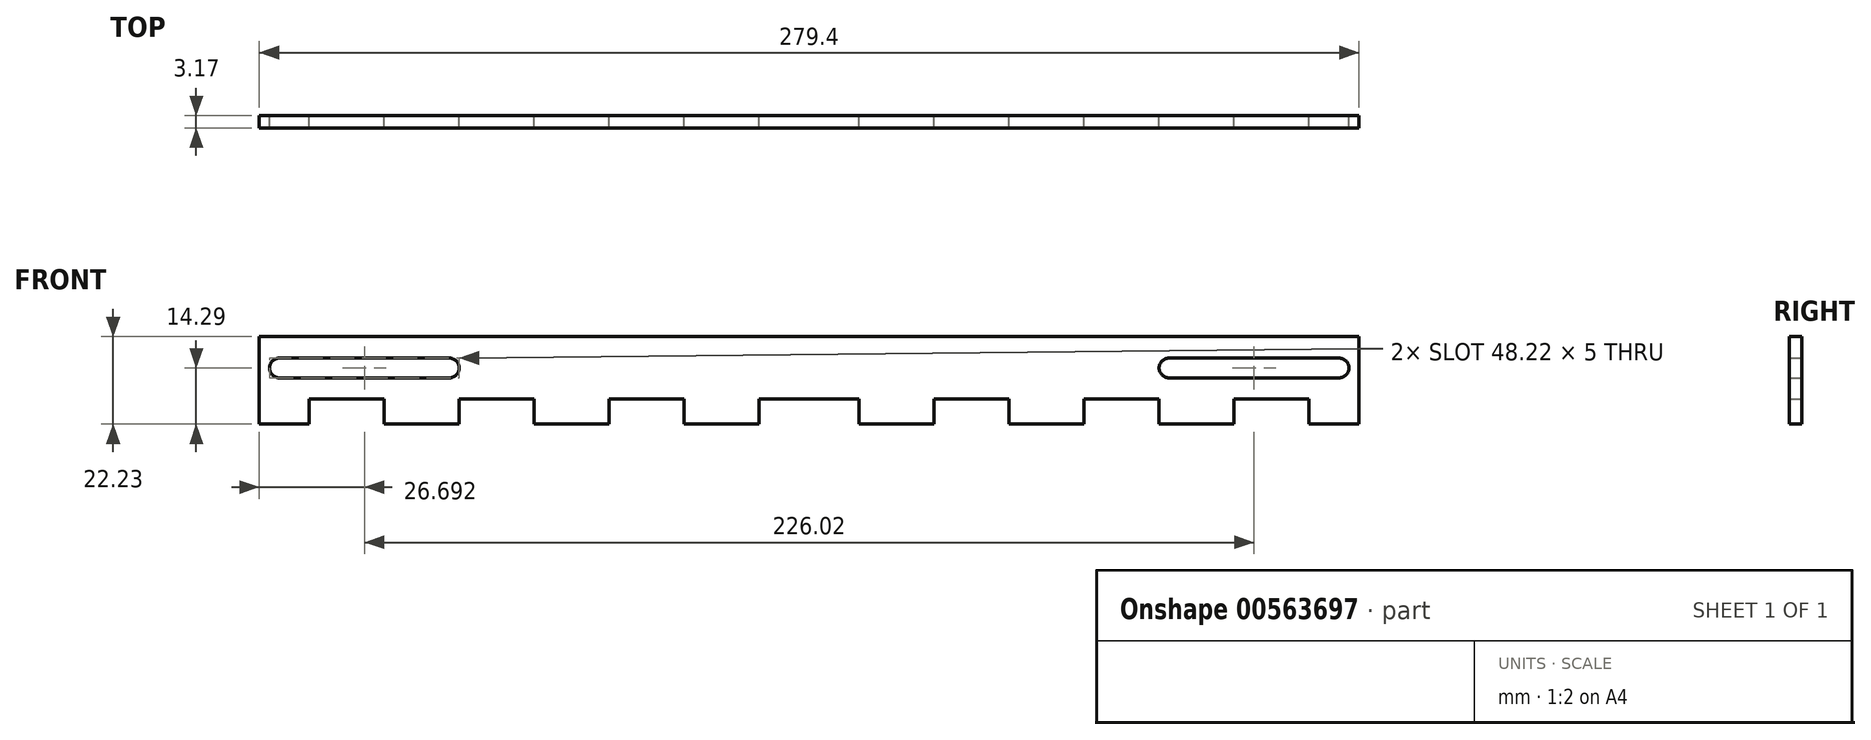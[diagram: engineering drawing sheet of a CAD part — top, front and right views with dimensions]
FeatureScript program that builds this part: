
annotation { "Feature Type Name" : "Feature", "Feature Type Description" : "" }
export const myFeature = defineFeature(function(context is Context, id is Id, definition is map)
    precondition{}
    {
        {
            var Q0;
            Q0=qCreatedBy(makeId("Front.planeOp"),FACE);
            var sketch = newSketch(context, id + "F0", { "sketchPlane" : qUnion([Q0])});
            skLineSegment(sketch, "E0", {"start": v(-38.69, 19.05) * mm, "end": v(-38.69, -20.37) * mm, "construction": true});
            skLineSegment(sketch, "E1", {"start": v(-165.69, -7.94) * mm, "end": v(-165.69, -1.59) * mm});
            skLineSegment(sketch, "E2", {"start": v(-165.69, -1.59) * mm, "end": v(-146.64, -1.59) * mm});
            skLineSegment(sketch, "E3.1.0.0", {"start": v(-146.64, -1.59) * mm, "end": v(-146.64, -7.94) * mm});
            skLineSegment(sketch, "E3.1.0.1", {"start": v(-146.64, -7.94) * mm, "end": v(-127.59, -7.94) * mm});
            skLineSegment(sketch, "E3.1.0.2", {"start": v(-127.59, -7.94) * mm, "end": v(-127.59, -1.59) * mm});
            skLineSegment(sketch, "E3.1.0.3", {"start": v(-127.59, -1.59) * mm, "end": v(-108.54, -1.59) * mm});
            skLineSegment(sketch, "E3.2.0.0", {"start": v(-108.54, -1.59) * mm, "end": v(-108.54, -7.94) * mm});
            skLineSegment(sketch, "E3.2.0.1", {"start": v(-108.54, -7.94) * mm, "end": v(-89.49, -7.94) * mm});
            skLineSegment(sketch, "E3.2.0.2", {"start": v(-89.49, -7.94) * mm, "end": v(-89.49, -1.59) * mm});
            skLineSegment(sketch, "E3.2.0.3", {"start": v(-89.49, -1.59) * mm, "end": v(-70.44, -1.59) * mm});
            skLineSegment(sketch, "E3.3.0.0", {"start": v(-70.44, -1.59) * mm, "end": v(-70.44, -7.94) * mm});
            skLineSegment(sketch, "E3.3.0.1", {"start": v(-70.44, -7.94) * mm, "end": v(-51.39, -7.94) * mm});
            skLineSegment(sketch, "E3.3.0.2", {"start": v(-51.39, -7.94) * mm, "end": v(-51.39, -1.59) * mm});
            skLineSegment(sketch, "E4.MirrorCS", {"start": v(12.11, -7.94) * mm, "end": v(12.11, -1.59) * mm});
            skLineSegment(sketch, "E5.MirrorCS", {"start": v(-6.94, -1.59) * mm, "end": v(-6.94, -7.94) * mm});
            skLineSegment(sketch, "E6.MirrorCS", {"start": v(69.26, -1.59) * mm, "end": v(69.26, -7.94) * mm});
            skLineSegment(sketch, "E7.MirrorCS", {"start": v(50.21, -7.94) * mm, "end": v(50.21, -1.59) * mm});
            skLineSegment(sketch, "E8.MirrorCS", {"start": v(31.16, -1.59) * mm, "end": v(31.16, -7.94) * mm});
            skLineSegment(sketch, "E9.MirrorCS", {"start": v(88.31, -7.94) * mm, "end": v(88.31, -1.59) * mm});
            skLineSegment(sketch, "E10.MirrorCS", {"start": v(-25.99, -7.94) * mm, "end": v(-25.99, -1.59) * mm});
            skLineSegment(sketch, "E11.MirrorCS", {"start": v(-6.94, -7.94) * mm, "end": v(-25.99, -7.94) * mm});
            skLineSegment(sketch, "E12.MirrorCS", {"start": v(88.31, -1.59) * mm, "end": v(69.26, -1.59) * mm});
            skLineSegment(sketch, "E13.MirrorCS", {"start": v(12.11, -1.59) * mm, "end": v(-6.94, -1.59) * mm});
            skLineSegment(sketch, "E14.MirrorCS", {"start": v(50.21, -1.59) * mm, "end": v(31.16, -1.59) * mm});
            skLineSegment(sketch, "E15.MirrorCS", {"start": v(31.16, -7.94) * mm, "end": v(12.11, -7.94) * mm});
            skLineSegment(sketch, "E16.MirrorCS", {"start": v(69.26, -7.94) * mm, "end": v(50.21, -7.94) * mm});
            skLineSegment(sketch, "E17", {"start": v(-51.39, -1.59) * mm, "end": v(-25.99, -1.59) * mm});
            skLineSegment(sketch, "E18", {"start": v(-38.69, 6.35) * mm, "end": v(-127.59, 6.35) * mm, "construction": true});
            skArc(sketch, "E19", {"start": v(-130.09, 8.85) * mm, "mid": v(-127.59, 6.35) * mm, "end": v(-130.09, 3.85) * mm});
            skLineSegment(sketch, "E20", {"start": v(-130.09, 8.85) * mm, "end": v(-173.3, 8.85) * mm});
            skLineSegment(sketch, "E21", {"start": v(-130.09, 3.85) * mm, "end": v(-173.3, 3.85) * mm});
            skArc(sketch, "E22", {"start": v(-173.3, 3.85) * mm, "mid": v(-175.8, 6.35) * mm, "end": v(-173.3, 8.85) * mm});
            skLineSegment(sketch, "E23.MirrorCS", {"start": v(52.71, 8.85) * mm, "end": v(95.93, 8.85) * mm});
            skLineSegment(sketch, "E24.MirrorCS", {"start": v(52.71, 3.85) * mm, "end": v(95.93, 3.85) * mm});
            skArc(sketch, "E25.MirrorCS", {"start": v(95.93, 3.85) * mm, "mid": v(98.43, 6.35) * mm, "end": v(95.93, 8.85) * mm});
            skArc(sketch, "E26.MirrorCS", {"start": v(52.71, 8.85) * mm, "mid": v(50.21, 6.35) * mm, "end": v(52.71, 3.85) * mm});
            skLineSegment(sketch, "E27", {"start": v(-178.39, 14.29) * mm, "end": v(-178.39, -7.94) * mm});
            skLineSegment(sketch, "E28", {"start": v(-178.39, 14.29) * mm, "end": v(101.01, 14.29) * mm});
            skLineSegment(sketch, "E29", {"start": v(-178.39, -7.94) * mm, "end": v(-165.69, -7.94) * mm});
            skLineSegment(sketch, "E30.MirrorCS", {"start": v(101.01, 14.29) * mm, "end": v(101.01, -7.94) * mm});
            skLineSegment(sketch, "E31", {"start": v(101.01, -7.94) * mm, "end": v(88.31, -7.94) * mm});
            skSolve(sketch);
        }
        {
            var Q0;
            Q0=makeQuery(id+"F0.imprint","IMPRINT",FACE,{"disambiguationData":[TD([[makeQuery(id+"F0.imprint","IMPRINT",EDGE,{"derivedFrom":sQuery(id+"F0.wireOp",EDGE,"E1")}),1.0]])]});
            extrude(context, id + "F1", {"entities" : qUnion([Q0]), "depth" : 3.17 * mm, "offsetDistance" : 25.4 * mm});
        }
    });
